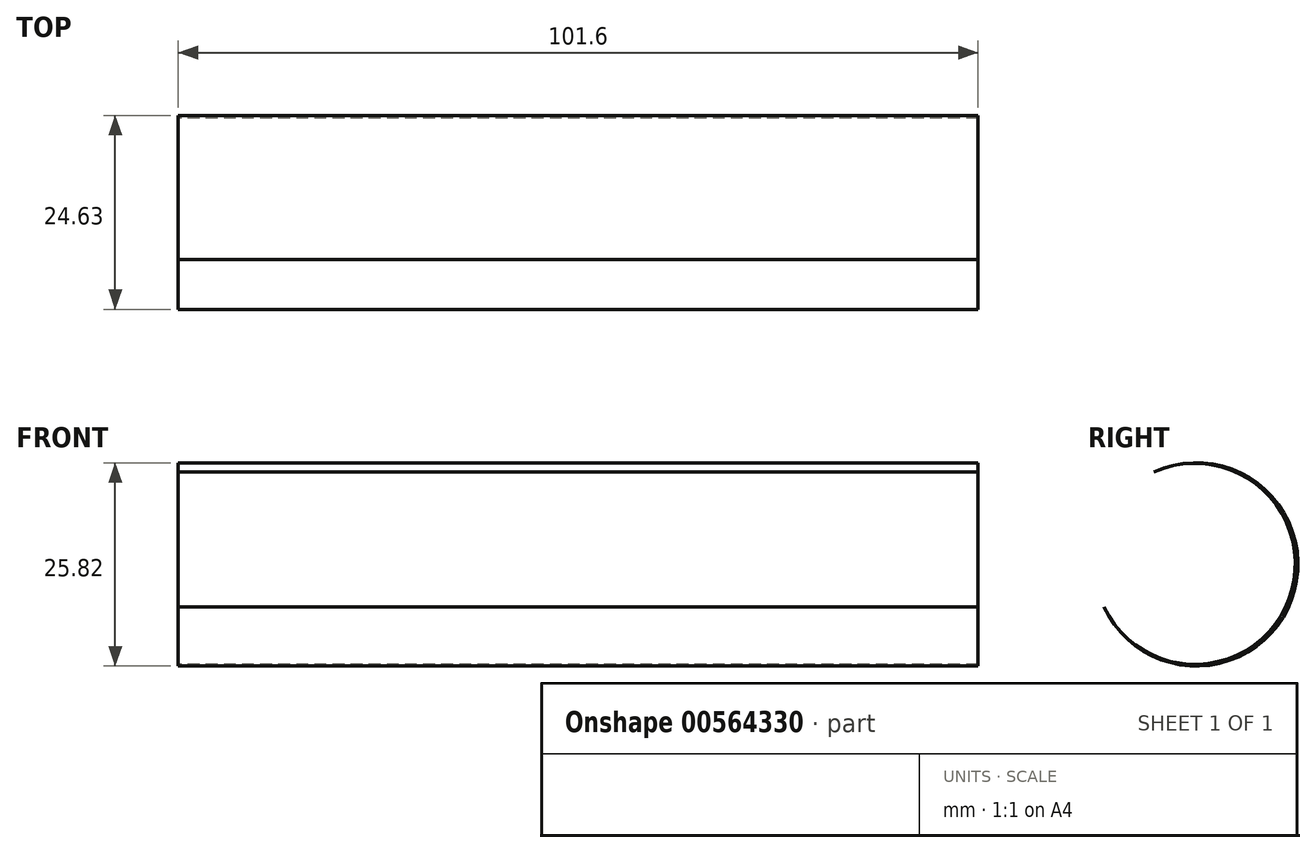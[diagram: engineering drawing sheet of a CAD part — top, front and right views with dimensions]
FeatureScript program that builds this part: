
annotation { "Feature Type Name" : "Feature", "Feature Type Description" : "" }
export const myFeature = defineFeature(function(context is Context, id is Id, definition is map)
    precondition{}
    {
        {
            var Q0;
            Q0=qCreatedBy(makeId("Right.planeOp"),FACE);
            cPlane(context, id + "F0", {"entities" : qUnion([Q0]), "cplaneType" : CPlaneType.OFFSET, "offset" : 109.98 * mm, "width" : 152.4 * mm, "height" : 152.4 * mm});
        }
        {
            var Q0;
            Q0=qCreatedBy(id+"F0.planeOp",FACE);
            var sketch = newSketch(context, id + "F1", { "sketchPlane" : qUnion([Q0])});
            skLineSegment(sketch, "E0", {"start": v(-40, 32.52) * mm, "end": v(-40, -40.87) * mm});
            skLineSegment(sketch, "E1", {"start": v(-40, -40.87) * mm, "end": v(57.56, -40.87) * mm});
            skLineSegment(sketch, "E2", {"start": v(57.56, -40.87) * mm, "end": v(57.56, 32.52) * mm});
            skLineSegment(sketch, "E3", {"start": v(57.56, 32.52) * mm, "end": v(-40, 32.52) * mm});
            skLineSegment(sketch, "E4", {"start": v(-40, 32.52) * mm, "end": v(57.56, -40.87) * mm});
            skSolve(sketch);
        }
        {
            var Q0;
            Q0=makeQuery(id+"F1.imprint","IMPRINT",FACE,{"disambiguationData":[TD([[makeQuery(id+"F1.imprint","IMPRINT",EDGE,{"derivedFrom":sQuery(id+"F1.wireOp",EDGE,"E0")}),1.0]])]});
            extrude(context, id + "F2", {"entities" : qUnion([Q0]), "oppositeDirection" : true, "depth" : 127 * mm, "offsetDistance" : 25.4 * mm});
        }
        {
            var Q0;
            Q0=makeQuery(id+"F1.imprint","IMPRINT",FACE,{"disambiguationData":[TD([[makeQuery(id+"F1.imprint","IMPRINT",EDGE,{"derivedFrom":sQuery(id+"F1.wireOp",EDGE,"E2")}),1.0]])]});
            extrude(context, id + "F3", {"entities" : qUnion([Q0]), "depth" : 127 * mm, "offsetDistance" : 25.4 * mm});
        }
        {
            var Q0;
            Q0=qCreatedBy(id+"F0.planeOp",FACE);
            var sketch = newSketch(context, id + "F4", { "sketchPlane" : qUnion([Q0])});
            skCircle(sketch, "E5", {"center": v(24.3, 11.9) * mm, "radius": 12.76 * mm});
            skSolve(sketch);
        }
        {
            var Q0;
            Q0 = qSketchRegion(id + "F4", true);
            extrude(context, id + "F5", {"entities" : qUnion([Q0]), "operationType" : NewBodyOperationType.REMOVE, "depth" : 127 * mm, "offsetDistance" : 25.4 * mm});
        }
        {
            var Q0;
            Q0=qCreatedBy(id+"F0.planeOp",FACE);
            var sketch = newSketch(context, id + "F6", { "sketchPlane" : qUnion([Q0])});
            skCircle(sketch, "E6", {"center": v(24.5, 11.83) * mm, "radius": 12.9 * mm});
            skSolve(sketch);
        }
        {
            var Q0;
            Q0 = qSketchRegion(id + "F6", true);
            extrude(context, id + "F7", {"entities" : qUnion([Q0]), "operationType" : NewBodyOperationType.INTERSECT, "depth" : 101.6 * mm, "offsetDistance" : 25.4 * mm});
        }
    });
